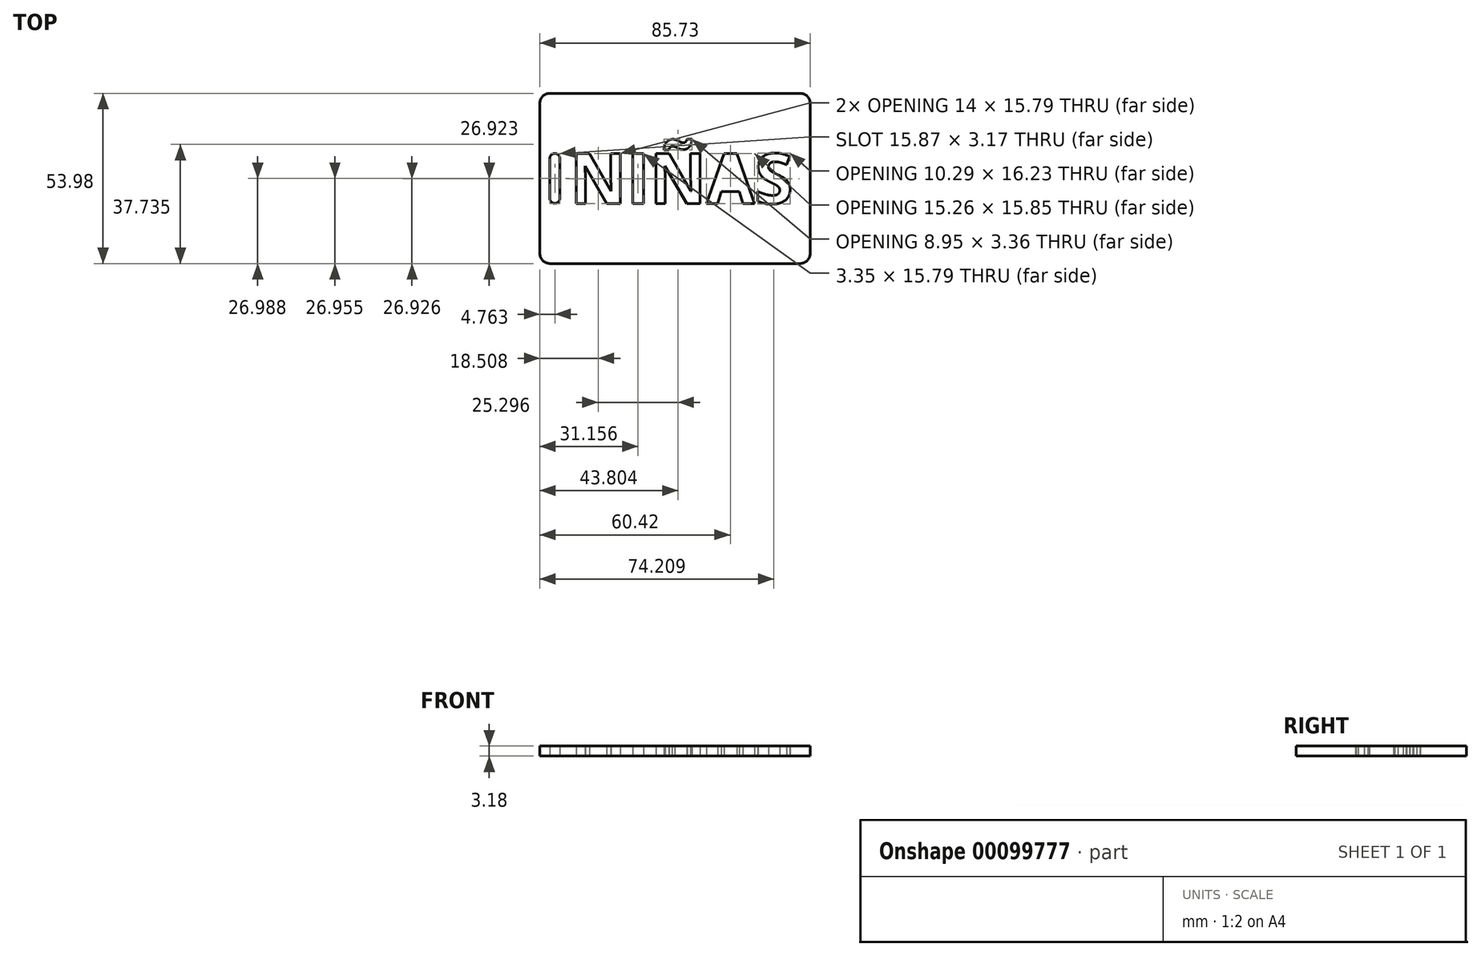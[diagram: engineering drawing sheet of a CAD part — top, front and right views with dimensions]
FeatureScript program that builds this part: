
annotation { "Feature Type Name" : "Feature", "Feature Type Description" : "" }
export const myFeature = defineFeature(function(context is Context, id is Id, definition is map)
    precondition{}
    {
        {
            var Q0;
            Q0=qCreatedBy(makeId("Top.planeOp"),FACE);
            var sketch = newSketch(context, id + "F0", { "sketchPlane" : qUnion([Q0])});
            skLineSegment(sketch, "E0.bottom", {"start": v(3.17, 0) * mm, "end": v(82.55, 0) * mm});
            skLineSegment(sketch, "E0.top", {"start": v(3.17, 53.98) * mm, "end": v(82.55, 53.97) * mm});
            skLineSegment(sketch, "E0.left", {"start": v(0, 3.18) * mm, "end": v(0, 50.8) * mm});
            skLineSegment(sketch, "E0.right", {"start": v(85.73, 3.18) * mm, "end": v(85.73, 50.8) * mm});
            skPoint(sketch, "E1.visualSharp", {"position": v(0, 53.98) * mm});
            skArc(sketch, "E1.filletArc", {"start": v(3.17, 53.98) * mm, "mid": v(0.93, 53.05) * mm, "end": v(0, 50.8) * mm});
            skPoint(sketch, "E2.visualSharp", {"position": v(85.72, 53.97) * mm});
            skArc(sketch, "E2.filletArc", {"start": v(85.73, 50.8) * mm, "mid": v(84.8, 53.05) * mm, "end": v(82.55, 53.97) * mm});
            skPoint(sketch, "E3.visualSharp", {"position": v(85.73, 0) * mm});
            skArc(sketch, "E3.filletArc", {"start": v(82.55, 0) * mm, "mid": v(84.8, 0.93) * mm, "end": v(85.73, 3.18) * mm});
            skPoint(sketch, "E4.visualSharp", {"position": v(0, 0) * mm});
            skArc(sketch, "E4.filletArc", {"start": v(0, 3.17) * mm, "mid": v(0.93, 0.93) * mm, "end": v(3.17, 0) * mm});
            skLineSegment(sketch, "E5", {"start": v(3.17, 33.34) * mm, "end": v(3.17, 20.64) * mm});
            skLineSegment(sketch, "E6", {"start": v(6.35, 33.34) * mm, "end": v(6.35, 20.64) * mm});
            skLineSegment(sketch, "E7", {"start": v(0, 26.99) * mm, "end": v(3.17, 26.99) * mm});
            skPoint(sketch, "E7.endSnap0", {"position": v(0, 26.99) * mm});
            skArc(sketch, "E8", {"start": v(6.35, 33.34) * mm, "mid": v(4.76, 34.93) * mm, "end": v(3.17, 33.34) * mm});
            skArc(sketch, "E9", {"start": v(3.17, 20.64) * mm, "mid": v(4.76, 19.05) * mm, "end": v(6.35, 20.64) * mm});
            skText(sketch, "E10", { "text": "NIÑAS", "fontName": "OpenSans-Bold.ttf"});
            skLineSegment(sketch, "E11", {"start": v(6.35, 26.99) * mm, "end": v(9.53, 26.99) * mm});
            const initialGuessF0  = {"E10": [0.00952, 0.01903, 1, 0, 0.01592]};
            skSetInitialGuess(sketch, initialGuessF0);
            skSolve(sketch);
        }
        {
            var Q0;
            Q0=makeQuery(id+"F0.imprint","IMPRINT",FACE,{"disambiguationData":[TD([[makeQuery(id+"F0.imprint","IMPRINT",EDGE,{"derivedFrom":sQuery(id+"F0.wireOp",EDGE,"E0.bottom")}),1.0]])]});
            extrude(context, id + "F1", {"entities" : qUnion([Q0]), "depth" : 3.17 * mm});
        }
    });
